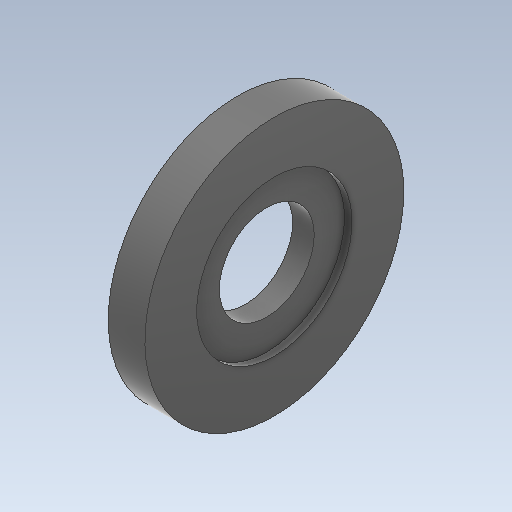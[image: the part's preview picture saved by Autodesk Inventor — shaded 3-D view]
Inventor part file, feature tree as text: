
AUTODESK INVENTOR PART (.ipt)
format: ipt  version: 2020 (Build 240168000, 168)  size: 120,832 bytes
history: native  units: mm
features: extrude x2, sketch x2, other x1
ambient origin geometry x8: Origin, YZ Plane, XZ Plane, XY Plane, X Axis, Y Axis, Z Axis, Center Point
bodies: Body1 (feature_tree)
feature tree (5):
  other  "Твердое тело1"
  extrude  "Выдавливание1"  Depth=11.0mm
  extrude  "Выдавливание2"  Depth=18.0mm
  sketch  "Эскиз1"
  sketch  "Эскиз2"
